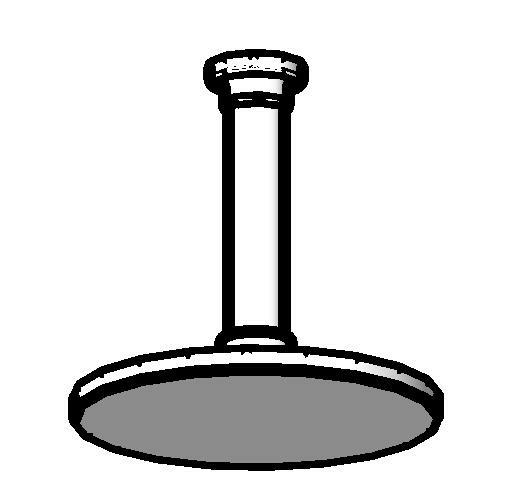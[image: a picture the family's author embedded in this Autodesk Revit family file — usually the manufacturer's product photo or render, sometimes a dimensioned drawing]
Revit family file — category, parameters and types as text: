
# Revit family: Deca_Chuveiro com tubo de teto_Aquamax_1998.TET
name_source: partatom
category: Plumbing Fixtures
units: mm (PartAtom-declared; Revit-internal decimal feet)

## family parameters
Cut with Voids When Loaded = No
Host = Face
Part Type = Normal
Room Calculation Point = No
Round Connector Dimension = Use Radius
Shared = No

## types (5) — shared parameters
Acompanha o Produto = Acompanha Deca confort (12l/min)
Aprovado por = quattroD
Atendimento ao Cliente = 0800-0117073
Categoria = CHUVEIROS E DUCHAS
Composição Anel Vedação = -
Composição Assento = -
Composição Básica = Liga de Cobre (bronze e latão),Plásticos de Engenharia,Elastômeros
Composição Componente = -
Consumo = -
Cor Interna = -
Cor Secundária = -
Cores Componente = -
Criado por = quattroD
Código Pai = 1998.TET
Description = Chuveiro com tubo de teto
Diâmetro Água Fria = 15 mm  [stored 0.0492126 ft]
Informações Complementares = -
Itens de Instalação = -
Linha = Banho Luxo
Manufacturer = Deca
Norma = NBR15206
Pressão máx. funcionamento = 40 MCA
Pressão mín. Aquec. Acúmulo = 2 MCA
Pressão mín. Aquec. Passagem = 8 MCA
Pressão mín. funcionamento = 2 MCA
Raio Água Fria = 8 mm  [stored 0.0262467 ft]
Saída de Esgoto = -
Segmento = Banheiro Luxo
Tipo de dispositivo economizador = Sim
Tipo de mecanismo utilizado = -
Tipo de rosca de entrada = BSP NBR 8133
Tipo de rosca de saída = -
URL = www.deca.com.br
Vazão na Pressão máx. (L/min) = 52
Vazão na Pressão mín. (L/min) = 12
zero-valued in all types: Default Elevation, HWFU, WFU

## per-type parameters (varying)
| type | Cor Principal | Material | Model | Peso Líquido (Kg) |
| 1998.C.TET_Cromado | Cromado | Deca_Cromado | 1998.C.TET | 2.458 |
| 1998.BL.TET.MT_Black Matte | Black Matte | Deca_Black Matte | 1998.BL.TET.MT | 2.874 |
| 1998.CT.TET.MT_Corten | Corten | Deca_Corten | 1998.CT.TET.MT | 2.874 |
| 1998.GL.TET.MT_Gold Matte | Gold Matte | Deca_Gold Matte | 1998.GL.TET.MT | 2.874 |
| 1998.GL.TET.RD_Red Gold | Red Gold | Deca_Red Gold | 1998.GL.TET.RD | 2.5 |

note: source unit labels omitted for Vazão na Pressão máx. (L/min), Vazão na Pressão mín. (L/min) — the stored unit's dimension contradicts the parameter name (converter mislabeling)

note: [stored X ft] marks values corroborated as IEEE doubles in the binary element streams (Revit-internal decimal feet)

## geometry (parser evidence)
native form markers: Sweep x2
no freeform markers — native parametric forms only
